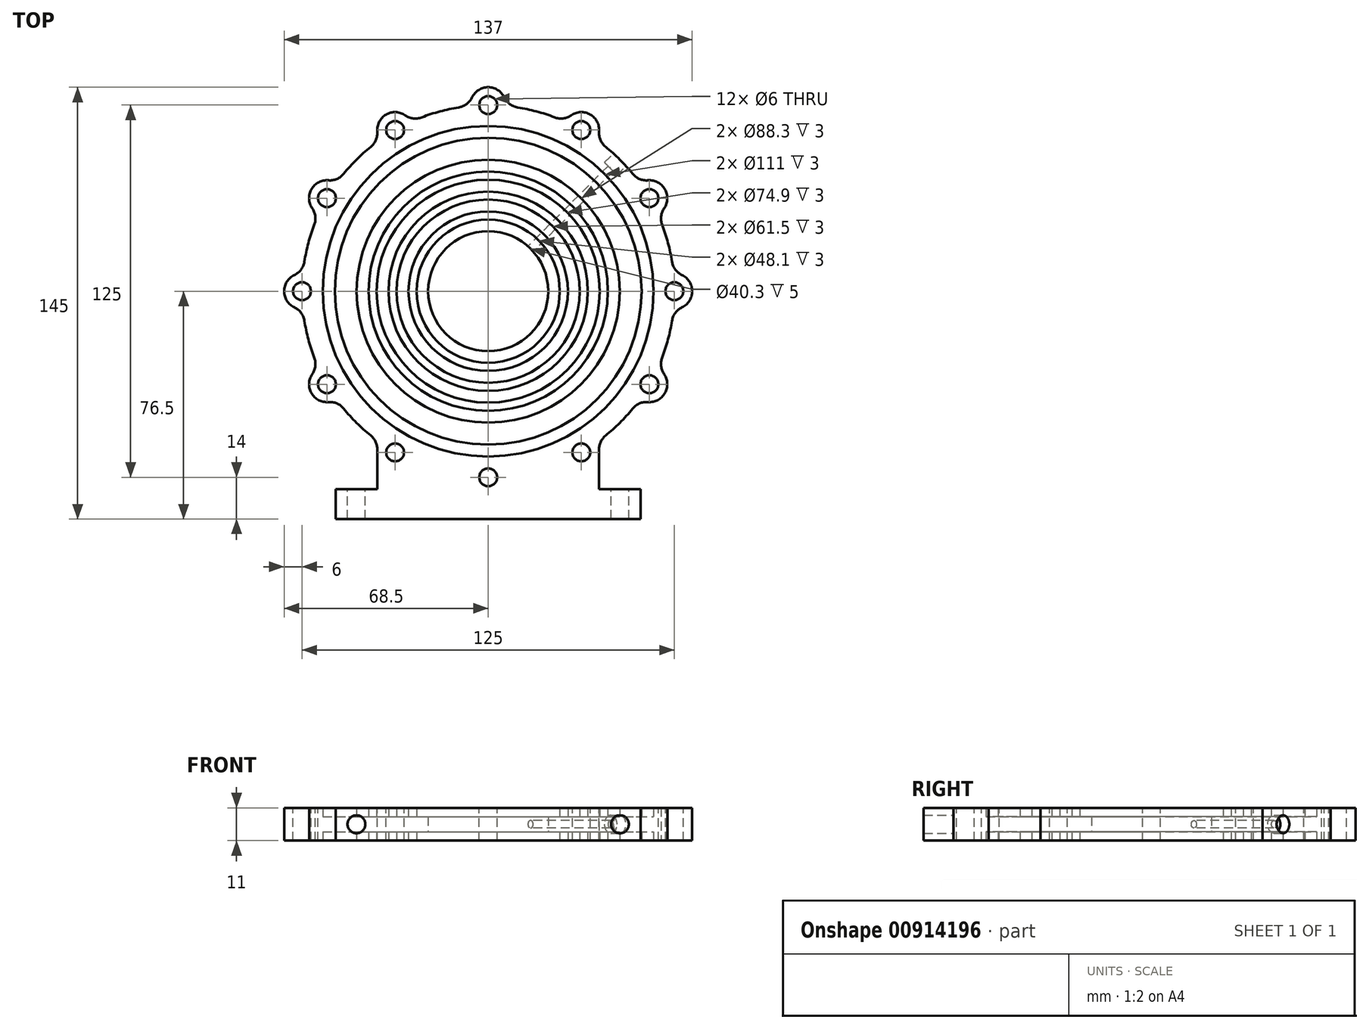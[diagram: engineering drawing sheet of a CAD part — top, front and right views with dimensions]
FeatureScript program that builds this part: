
annotation { "Feature Type Name" : "Feature", "Feature Type Description" : "" }
export const myFeature = defineFeature(function(context is Context, id is Id, definition is map)
    precondition{}
    {
        {
            var Q0;
            Q0=qCreatedBy(makeId("Front.planeOp"),FACE);
            var sketch = newSketch(context, id + "F0", { "sketchPlane" : qUnion([Q0])});
            skLineSegment(sketch, "E0", {"start": v(0, 7.63) * mm, "end": v(0, -7.62) * mm, "construction": true});
            skLineSegment(sketch, "E1", {"start": v(12.5, -2.15) * mm, "end": v(47.5, -2.15) * mm, "construction": true});
            skLineSegment(sketch, "E2", {"start": v(47.5, -2.15) * mm, "end": v(47.5, -0.65) * mm, "construction": true});
            skLineSegment(sketch, "E3", {"start": v(47.5, -0.65) * mm, "end": v(43.5, -0.65) * mm, "construction": true});
            skLineSegment(sketch, "E4", {"start": v(43.5, -0.65) * mm, "end": v(43.5, 2.35) * mm, "construction": true});
            skLineSegment(sketch, "E5", {"start": v(43.5, 2.35) * mm, "end": v(40.8, 2.35) * mm, "construction": true});
            skLineSegment(sketch, "E6", {"start": v(40.8, 2.35) * mm, "end": v(40.8, -0.65) * mm, "construction": true});
            skLineSegment(sketch, "E7", {"start": v(40.8, -0.65) * mm, "end": v(36.8, -0.65) * mm, "construction": true});
            skLineSegment(sketch, "E8", {"start": v(36.8, -0.65) * mm, "end": v(36.8, 2.35) * mm, "construction": true});
            skLineSegment(sketch, "E9", {"start": v(36.8, 2.35) * mm, "end": v(34.1, 2.35) * mm, "construction": true});
            skLineSegment(sketch, "E10", {"start": v(34.1, 2.35) * mm, "end": v(34.1, -0.65) * mm, "construction": true});
            skLineSegment(sketch, "E11", {"start": v(34.1, -0.65) * mm, "end": v(30.1, -0.65) * mm, "construction": true});
            skLineSegment(sketch, "E12", {"start": v(30.1, -0.65) * mm, "end": v(30.1, 2.35) * mm, "construction": true});
            skLineSegment(sketch, "E13", {"start": v(30.1, 2.35) * mm, "end": v(27.4, 2.35) * mm, "construction": true});
            skLineSegment(sketch, "E14", {"start": v(27.4, 2.35) * mm, "end": v(27.4, -0.65) * mm, "construction": true});
            skLineSegment(sketch, "E15", {"start": v(27.4, -0.65) * mm, "end": v(23.4, -0.65) * mm, "construction": true});
            skLineSegment(sketch, "E16", {"start": v(23.4, -0.65) * mm, "end": v(23.4, 2.35) * mm, "construction": true});
            skLineSegment(sketch, "E17", {"start": v(23.4, 2.35) * mm, "end": v(19.5, 2.35) * mm, "construction": true});
            skLineSegment(sketch, "E18", {"start": v(19.5, 2.35) * mm, "end": v(19.5, -0.65) * mm, "construction": true});
            skLineSegment(sketch, "E19", {"start": v(19.5, -0.65) * mm, "end": v(12.5, -0.65) * mm, "construction": true});
            skLineSegment(sketch, "E20", {"start": v(12.5, -0.65) * mm, "end": v(12.5, -2.15) * mm, "construction": true});
            skLineSegment(sketch, "E21.0", {"start": v(24.05, 3) * mm, "end": v(20.15, 3) * mm});
            skLineSegment(sketch, "E21.1", {"start": v(24.05, 0) * mm, "end": v(24.05, 3) * mm});
            skLineSegment(sketch, "E21.2", {"start": v(26.75, 0) * mm, "end": v(24.05, 0) * mm});
            skLineSegment(sketch, "E21.3", {"start": v(26.75, 3) * mm, "end": v(26.75, 0) * mm});
            skLineSegment(sketch, "E21.4", {"start": v(30.75, 3) * mm, "end": v(26.75, 3) * mm});
            skLineSegment(sketch, "E21.5", {"start": v(40.15, 3) * mm, "end": v(40.15, 0) * mm});
            skLineSegment(sketch, "E21.6", {"start": v(44.15, 3) * mm, "end": v(40.15, 3) * mm});
            skLineSegment(sketch, "E21.7", {"start": v(44.15, 0) * mm, "end": v(44.15, 3) * mm});
            skLineSegment(sketch, "E21.8", {"start": v(62.5, 0) * mm, "end": v(55.5, 0) * mm});
            skLineSegment(sketch, "E21.9", {"start": v(40.15, 0) * mm, "end": v(37.45, 0) * mm});
            skLineSegment(sketch, "E21.10", {"start": v(37.45, 0) * mm, "end": v(37.45, 3) * mm});
            skLineSegment(sketch, "E21.11", {"start": v(37.45, 3) * mm, "end": v(33.45, 3) * mm});
            skLineSegment(sketch, "E21.12", {"start": v(33.45, 3) * mm, "end": v(33.45, 0) * mm});
            skLineSegment(sketch, "E21.13", {"start": v(33.45, 0) * mm, "end": v(30.75, 0) * mm});
            skLineSegment(sketch, "E21.14", {"start": v(30.75, 0) * mm, "end": v(30.75, 3) * mm});
            skLineSegment(sketch, "E22", {"start": v(51.5, 0) * mm, "end": v(51.5, 3) * mm});
            skLineSegment(sketch, "E23", {"start": v(51.5, 3) * mm, "end": v(55.5, 3) * mm});
            skLineSegment(sketch, "E24", {"start": v(55.5, 3) * mm, "end": v(55.5, 0) * mm});
            skLineSegment(sketch, "E25.trimOffspring", {"start": v(51.5, 0) * mm, "end": v(44.15, 0) * mm});
            skLineSegment(sketch, "E26", {"start": v(20.15, 5.5) * mm, "end": v(20.15, 3) * mm});
            skLineSegment(sketch, "E27", {"start": v(62.5, 5.5) * mm, "end": v(62.5, 0) * mm});
            skLineSegment(sketch, "E28", {"start": v(20.15, 5.5) * mm, "end": v(62.5, 5.5) * mm, "construction": true});
            skLineSegment(sketch, "E29.MirrorCS", {"start": v(0, 3.37) * mm, "end": v(0, 18.62) * mm, "construction": true});
            skLineSegment(sketch, "E30.MirrorCS", {"start": v(47.5, 13.15) * mm, "end": v(47.5, 11.65) * mm, "construction": true});
            skLineSegment(sketch, "E31.MirrorCS", {"start": v(12.5, 13.15) * mm, "end": v(47.5, 13.15) * mm, "construction": true});
            skLineSegment(sketch, "E32.MirrorCS", {"start": v(26.75, 8) * mm, "end": v(26.75, 11) * mm});
            skLineSegment(sketch, "E33.MirrorCS", {"start": v(23.4, 8.65) * mm, "end": v(19.5, 8.65) * mm, "construction": true});
            skLineSegment(sketch, "E34.MirrorCS", {"start": v(36.8, 8.65) * mm, "end": v(34.1, 8.65) * mm, "construction": true});
            skLineSegment(sketch, "E35.MirrorCS", {"start": v(27.4, 8.65) * mm, "end": v(27.4, 11.65) * mm, "construction": true});
            skLineSegment(sketch, "E36.MirrorCS", {"start": v(37.45, 8) * mm, "end": v(33.45, 8) * mm});
            skLineSegment(sketch, "E37.MirrorCS", {"start": v(20.15, 5.5) * mm, "end": v(20.15, 8) * mm});
            skLineSegment(sketch, "E38.MirrorCS", {"start": v(40.15, 8) * mm, "end": v(40.15, 11) * mm});
            skLineSegment(sketch, "E39.MirrorCS", {"start": v(44.15, 8) * mm, "end": v(40.15, 8) * mm});
            skLineSegment(sketch, "E40.MirrorCS", {"start": v(33.45, 8) * mm, "end": v(33.45, 11) * mm});
            skLineSegment(sketch, "E41.MirrorCS", {"start": v(24.05, 8) * mm, "end": v(20.15, 8) * mm});
            skLineSegment(sketch, "E42.MirrorCS", {"start": v(36.8, 11.65) * mm, "end": v(36.8, 8.65) * mm, "construction": true});
            skLineSegment(sketch, "E43.MirrorCS", {"start": v(40.15, 11) * mm, "end": v(37.45, 11) * mm});
            skLineSegment(sketch, "E44.MirrorCS", {"start": v(24.05, 11) * mm, "end": v(24.05, 8) * mm});
            skLineSegment(sketch, "E45.MirrorCS", {"start": v(12.5, 11.65) * mm, "end": v(12.5, 13.15) * mm, "construction": true});
            skLineSegment(sketch, "E46.MirrorCS", {"start": v(30.1, 8.65) * mm, "end": v(27.4, 8.65) * mm, "construction": true});
            skLineSegment(sketch, "E47.MirrorCS", {"start": v(30.75, 11) * mm, "end": v(30.75, 8) * mm});
            skLineSegment(sketch, "E48.MirrorCS", {"start": v(43.5, 11.65) * mm, "end": v(43.5, 8.65) * mm, "construction": true});
            skLineSegment(sketch, "E49.MirrorCS", {"start": v(55.5, 8) * mm, "end": v(55.5, 11) * mm});
            skLineSegment(sketch, "E50.MirrorCS", {"start": v(34.1, 11.65) * mm, "end": v(30.1, 11.65) * mm, "construction": true});
            skLineSegment(sketch, "E51.MirrorCS", {"start": v(40.8, 8.65) * mm, "end": v(40.8, 11.65) * mm, "construction": true});
            skLineSegment(sketch, "E52.MirrorCS", {"start": v(62.5, 5.5) * mm, "end": v(62.5, 11) * mm});
            skLineSegment(sketch, "E53.MirrorCS", {"start": v(37.45, 11) * mm, "end": v(37.45, 8) * mm});
            skLineSegment(sketch, "E54.MirrorCS", {"start": v(30.75, 8) * mm, "end": v(26.75, 8) * mm});
            skLineSegment(sketch, "E55.MirrorCS", {"start": v(23.4, 11.65) * mm, "end": v(23.4, 8.65) * mm, "construction": true});
            skLineSegment(sketch, "E56.MirrorCS", {"start": v(40.8, 11.65) * mm, "end": v(36.8, 11.65) * mm, "construction": true});
            skLineSegment(sketch, "E57.MirrorCS", {"start": v(47.5, 11.65) * mm, "end": v(43.5, 11.65) * mm, "construction": true});
            skLineSegment(sketch, "E58.MirrorCS", {"start": v(19.5, 8.65) * mm, "end": v(19.5, 11.65) * mm, "construction": true});
            skLineSegment(sketch, "E59.MirrorCS", {"start": v(30.1, 11.65) * mm, "end": v(30.1, 8.65) * mm, "construction": true});
            skLineSegment(sketch, "E60.MirrorCS", {"start": v(27.4, 11.65) * mm, "end": v(23.4, 11.65) * mm, "construction": true});
            skLineSegment(sketch, "E61.MirrorCS", {"start": v(26.75, 11) * mm, "end": v(24.05, 11) * mm});
            skLineSegment(sketch, "E62.MirrorCS", {"start": v(51.5, 11) * mm, "end": v(51.5, 8) * mm});
            skLineSegment(sketch, "E63.MirrorCS", {"start": v(51.5, 11) * mm, "end": v(44.15, 11) * mm});
            skLineSegment(sketch, "E64.MirrorCS", {"start": v(51.5, 8) * mm, "end": v(55.5, 8) * mm});
            skLineSegment(sketch, "E65.MirrorCS", {"start": v(44.15, 11) * mm, "end": v(44.15, 8) * mm});
            skLineSegment(sketch, "E66.MirrorCS", {"start": v(62.5, 11) * mm, "end": v(55.5, 11) * mm});
            skLineSegment(sketch, "E67.MirrorCS", {"start": v(34.1, 8.65) * mm, "end": v(34.1, 11.65) * mm, "construction": true});
            skLineSegment(sketch, "E68.MirrorCS", {"start": v(19.5, 11.65) * mm, "end": v(12.5, 11.65) * mm, "construction": true});
            skLineSegment(sketch, "E69.MirrorCS", {"start": v(33.45, 11) * mm, "end": v(30.75, 11) * mm});
            skLineSegment(sketch, "E70.MirrorCS", {"start": v(43.5, 8.65) * mm, "end": v(40.8, 8.65) * mm, "construction": true});
            skLineSegment(sketch, "E71", {"start": v(59.5, 11) * mm, "end": v(59.5, 0) * mm, "construction": true});
            skSolve(sketch);
        }
        {
            var Q0;
            Q0 = qSketchRegion(id + "F0", true);
            var Q1;
            Q1=sQuery(id+"F0.wireOp",EDGE,"E29.MirrorCS");
            revolve(context, id + "F1", {"surfaceOperationType" : NewSurfaceOperationType.NEW, "entities" : qUnion([Q0]), "axis" : qUnion([Q1]), "revolveType" : RevolveType.FULL});
        }
        {
            var Q0;
            Q0=makeQuery(id+"F1.opRevolve","SWEPT_FACE",FACE,{"disambiguationData":[OSD([sQuery(id+"F0.wireOp",EDGE,"E66.MirrorCS")])]});
            var sketch = newSketch(context, id + "F2", { "sketchPlane" : qUnion([Q0])});
            skCircle(sketch, "E72", {"center": v(0, 62.5) * mm, "radius": 6 * mm});
            skCircle(sketch, "E73.1.0", {"center": v(-31.25, 54.13) * mm, "radius": 6 * mm});
            skCircle(sketch, "E73.2.0", {"center": v(-54.13, 31.25) * mm, "radius": 6 * mm});
            skCircle(sketch, "E73.3.0", {"center": v(-62.5, 0) * mm, "radius": 6 * mm});
            skCircle(sketch, "E73.4.0", {"center": v(-54.13, -31.25) * mm, "radius": 6 * mm});
            skCircle(sketch, "E73.5.0", {"center": v(-31.25, -54.13) * mm, "radius": 6 * mm});
            skCircle(sketch, "E73.6.0", {"center": v(0, -62.5) * mm, "radius": 6 * mm});
            skCircle(sketch, "E73.7.0", {"center": v(31.25, -54.13) * mm, "radius": 6 * mm});
            skCircle(sketch, "E73.8.0", {"center": v(54.13, -31.25) * mm, "radius": 6 * mm});
            skCircle(sketch, "E73.9.0", {"center": v(62.5, 0) * mm, "radius": 6 * mm});
            skCircle(sketch, "E73.10.0", {"center": v(54.13, 31.25) * mm, "radius": 6 * mm});
            skCircle(sketch, "E73.11.0", {"center": v(31.25, 54.13) * mm, "radius": 6 * mm});
            skPoint(sketch, "E73.center", {"position": v(0, 0) * mm});
            skSolve(sketch);
        }
        {
            var Q0;
            Q0 = qSketchRegion(id + "F2", true);
            var Q1;
            Q1=makeQuery(id+"F1.opRevolve","SWEPT_FACE",FACE,{"disambiguationData":[OSD([sQuery(id+"F0.wireOp",EDGE,"E21.8")])]});
            extrude(context, id + "F3", {"entities" : qUnion([Q0]), "operationType" : NewBodyOperationType.ADD, "endBound" : BoundingType.UP_TO_SURFACE, "oppositeDirection" : true, "depth" : 10 * mm, "endBoundEntityFace" : qUnion([Q1]), "offsetDistance" : 25 * mm});
        }
        {
            var Q0;
            Q0=makeQuery(id+"F3.boolean.opBoolean","MERGE",FACE,{"derivedFrom":[makeQuery(id+"F1.opRevolve","SWEPT_FACE",FACE,{"disambiguationData":[OSD([sQuery(id+"F0.wireOp",EDGE,"E66.MirrorCS")])]}),makeQuery(id+"F3.opExtrude","CAP_FACE",FACE,{"disambiguationData":[OSD([sQuery(id+"F2.wireOp",EDGE,"E72")])],"isStart":true}),makeQuery(id+"F3.opExtrude","CAP_FACE",FACE,{"disambiguationData":[OSD([sQuery(id+"F2.wireOp",EDGE,"E73.1.0")])],"isStart":true}),makeQuery(id+"F3.opExtrude","CAP_FACE",FACE,{"disambiguationData":[OSD([sQuery(id+"F2.wireOp",EDGE,"E73.2.0")])],"isStart":true}),makeQuery(id+"F3.opExtrude","CAP_FACE",FACE,{"disambiguationData":[OSD([sQuery(id+"F2.wireOp",EDGE,"E73.3.0")])],"isStart":true}),makeQuery(id+"F3.opExtrude","CAP_FACE",FACE,{"disambiguationData":[OSD([sQuery(id+"F2.wireOp",EDGE,"E73.4.0")])],"isStart":true}),makeQuery(id+"F3.opExtrude","CAP_FACE",FACE,{"disambiguationData":[OSD([sQuery(id+"F2.wireOp",EDGE,"E73.5.0")])],"isStart":true}),makeQuery(id+"F3.opExtrude","CAP_FACE",FACE,{"disambiguationData":[OSD([sQuery(id+"F2.wireOp",EDGE,"E73.6.0")])],"isStart":true}),makeQuery(id+"F3.opExtrude","CAP_FACE",FACE,{"disambiguationData":[OSD([sQuery(id+"F2.wireOp",EDGE,"E73.7.0")])],"isStart":true}),makeQuery(id+"F3.opExtrude","CAP_FACE",FACE,{"disambiguationData":[OSD([sQuery(id+"F2.wireOp",EDGE,"E73.8.0")])],"isStart":true}),makeQuery(id+"F3.opExtrude","CAP_FACE",FACE,{"disambiguationData":[OSD([sQuery(id+"F2.wireOp",EDGE,"E73.9.0")])],"isStart":true}),makeQuery(id+"F3.opExtrude","CAP_FACE",FACE,{"disambiguationData":[OSD([sQuery(id+"F2.wireOp",EDGE,"E73.10.0")])],"isStart":true}),makeQuery(id+"F3.opExtrude","CAP_FACE",FACE,{"disambiguationData":[OSD([sQuery(id+"F2.wireOp",EDGE,"E73.11.0")])],"isStart":true})]});
            var sketch = newSketch(context, id + "F4", { "sketchPlane" : qUnion([Q0])});
            skCircle(sketch, "E74", {"center": v(0, 62.5) * mm, "radius": 3 * mm});
            skCircle(sketch, "E75.1.0", {"center": v(-31.25, 54.13) * mm, "radius": 3 * mm});
            skCircle(sketch, "E75.2.0", {"center": v(-54.13, 31.25) * mm, "radius": 3 * mm});
            skCircle(sketch, "E75.3.0", {"center": v(-62.5, 0) * mm, "radius": 3 * mm});
            skCircle(sketch, "E75.4.0", {"center": v(-54.13, -31.25) * mm, "radius": 3 * mm});
            skCircle(sketch, "E75.5.0", {"center": v(-31.25, -54.13) * mm, "radius": 3 * mm});
            skCircle(sketch, "E75.6.0", {"center": v(0, -62.5) * mm, "radius": 3 * mm});
            skCircle(sketch, "E75.7.0", {"center": v(31.25, -54.13) * mm, "radius": 3 * mm});
            skCircle(sketch, "E75.8.0", {"center": v(54.13, -31.25) * mm, "radius": 3 * mm});
            skCircle(sketch, "E75.9.0", {"center": v(62.5, 0) * mm, "radius": 3 * mm});
            skCircle(sketch, "E75.10.0", {"center": v(54.13, 31.25) * mm, "radius": 3 * mm});
            skCircle(sketch, "E75.11.0", {"center": v(31.25, 54.13) * mm, "radius": 3 * mm});
            skPoint(sketch, "E75.center", {"position": v(0, 0) * mm});
            skSolve(sketch);
        }
        {
            var Q0;
            Q0 = qSketchRegion(id + "F4", true);
            extrude(context, id + "F5", {"entities" : qUnion([Q0]), "operationType" : NewBodyOperationType.REMOVE, "endBound" : BoundingType.THROUGH_ALL, "oppositeDirection" : true, "depth" : 25 * mm, "offsetDistance" : 25 * mm});
        }
        {
            var Q0;
            Q0=makeQuery(id+"F3.boolean.opBoolean","INTERSECT",EDGE,{"disambiguationData":[OD(1.0)],"derivedFrom":[makeQuery(id+"F1.opRevolve","SWEPT_FACE",FACE,{"disambiguationData":[OSD([sQuery(id+"F0.wireOp",EDGE,"E27"),sQuery(id+"F0.wireOp",EDGE,"E52.MirrorCS")])]}),makeQuery(id+"F3.opExtrude","SWEPT_FACE",FACE,{"disambiguationData":[OSD([sQuery(id+"F2.wireOp",EDGE,"E73.8.0")])]})]});
            var Q1;
            Q1=makeQuery(id+"F3.boolean.opBoolean","INTERSECT",EDGE,{"disambiguationData":[OD(1.0)],"derivedFrom":[makeQuery(id+"F1.opRevolve","SWEPT_FACE",FACE,{"disambiguationData":[OSD([sQuery(id+"F0.wireOp",EDGE,"E27"),sQuery(id+"F0.wireOp",EDGE,"E52.MirrorCS")])]}),makeQuery(id+"F3.opExtrude","SWEPT_FACE",FACE,{"disambiguationData":[OSD([sQuery(id+"F2.wireOp",EDGE,"E73.7.0")])]})]});
            var Q2;
            Q2=makeQuery(id+"F3.boolean.opBoolean","INTERSECT",EDGE,{"disambiguationData":[OD(0.0)],"derivedFrom":[makeQuery(id+"F1.opRevolve","SWEPT_FACE",FACE,{"disambiguationData":[OSD([sQuery(id+"F0.wireOp",EDGE,"E27"),sQuery(id+"F0.wireOp",EDGE,"E52.MirrorCS")])]}),makeQuery(id+"F3.opExtrude","SWEPT_FACE",FACE,{"disambiguationData":[OSD([sQuery(id+"F2.wireOp",EDGE,"E73.9.0")])]})]});
            var Q3;
            Q3=makeQuery(id+"F3.boolean.opBoolean","INTERSECT",EDGE,{"disambiguationData":[OD(1.0)],"derivedFrom":[makeQuery(id+"F1.opRevolve","SWEPT_FACE",FACE,{"disambiguationData":[OSD([sQuery(id+"F0.wireOp",EDGE,"E27"),sQuery(id+"F0.wireOp",EDGE,"E52.MirrorCS")])]}),makeQuery(id+"F3.opExtrude","SWEPT_FACE",FACE,{"disambiguationData":[OSD([sQuery(id+"F2.wireOp",EDGE,"E73.9.0")])]})]});
            var Q4;
            Q4=makeQuery(id+"F3.boolean.opBoolean","INTERSECT",EDGE,{"disambiguationData":[OD(0.0)],"derivedFrom":[makeQuery(id+"F1.opRevolve","SWEPT_FACE",FACE,{"disambiguationData":[OSD([sQuery(id+"F0.wireOp",EDGE,"E27"),sQuery(id+"F0.wireOp",EDGE,"E52.MirrorCS")])]}),makeQuery(id+"F3.opExtrude","SWEPT_FACE",FACE,{"disambiguationData":[OSD([sQuery(id+"F2.wireOp",EDGE,"E73.8.0")])]})]});
            var Q5;
            Q5=makeQuery(id+"F3.boolean.opBoolean","INTERSECT",EDGE,{"disambiguationData":[OD(0.0)],"derivedFrom":[makeQuery(id+"F1.opRevolve","SWEPT_FACE",FACE,{"disambiguationData":[OSD([sQuery(id+"F0.wireOp",EDGE,"E27"),sQuery(id+"F0.wireOp",EDGE,"E52.MirrorCS")])]}),makeQuery(id+"F3.opExtrude","SWEPT_FACE",FACE,{"disambiguationData":[OSD([sQuery(id+"F2.wireOp",EDGE,"E73.7.0")])]})]});
            var Q6;
            Q6=makeQuery(id+"F3.boolean.opBoolean","INTERSECT",EDGE,{"disambiguationData":[OD(1.0)],"derivedFrom":[makeQuery(id+"F1.opRevolve","SWEPT_FACE",FACE,{"disambiguationData":[OSD([sQuery(id+"F0.wireOp",EDGE,"E27"),sQuery(id+"F0.wireOp",EDGE,"E52.MirrorCS")])]}),makeQuery(id+"F3.opExtrude","SWEPT_FACE",FACE,{"disambiguationData":[OSD([sQuery(id+"F2.wireOp",EDGE,"E73.6.0")])]})]});
            var Q7;
            Q7=makeQuery(id+"F3.boolean.opBoolean","INTERSECT",EDGE,{"disambiguationData":[OD(1.0)],"derivedFrom":[makeQuery(id+"F1.opRevolve","SWEPT_FACE",FACE,{"disambiguationData":[OSD([sQuery(id+"F0.wireOp",EDGE,"E27"),sQuery(id+"F0.wireOp",EDGE,"E52.MirrorCS")])]}),makeQuery(id+"F3.opExtrude","SWEPT_FACE",FACE,{"disambiguationData":[OSD([sQuery(id+"F2.wireOp",EDGE,"E73.5.0")])]})]});
            var Q8;
            Q8=makeQuery(id+"F3.boolean.opBoolean","INTERSECT",EDGE,{"disambiguationData":[OD(0.0)],"derivedFrom":[makeQuery(id+"F1.opRevolve","SWEPT_FACE",FACE,{"disambiguationData":[OSD([sQuery(id+"F0.wireOp",EDGE,"E27"),sQuery(id+"F0.wireOp",EDGE,"E52.MirrorCS")])]}),makeQuery(id+"F3.opExtrude","SWEPT_FACE",FACE,{"disambiguationData":[OSD([sQuery(id+"F2.wireOp",EDGE,"E73.6.0")])]})]});
            var Q9;
            Q9=makeQuery(id+"F3.boolean.opBoolean","INTERSECT",EDGE,{"disambiguationData":[OD(0.0)],"derivedFrom":[makeQuery(id+"F1.opRevolve","SWEPT_FACE",FACE,{"disambiguationData":[OSD([sQuery(id+"F0.wireOp",EDGE,"E27"),sQuery(id+"F0.wireOp",EDGE,"E52.MirrorCS")])]}),makeQuery(id+"F3.opExtrude","SWEPT_FACE",FACE,{"disambiguationData":[OSD([sQuery(id+"F2.wireOp",EDGE,"E73.5.0")])]})]});
            var Q10;
            Q10=makeQuery(id+"F3.boolean.opBoolean","INTERSECT",EDGE,{"disambiguationData":[OD(0.0)],"derivedFrom":[makeQuery(id+"F1.opRevolve","SWEPT_FACE",FACE,{"disambiguationData":[OSD([sQuery(id+"F0.wireOp",EDGE,"E27"),sQuery(id+"F0.wireOp",EDGE,"E52.MirrorCS")])]}),makeQuery(id+"F3.opExtrude","SWEPT_FACE",FACE,{"disambiguationData":[OSD([sQuery(id+"F2.wireOp",EDGE,"E73.4.0")])]})]});
            var Q11;
            Q11=makeQuery(id+"F3.boolean.opBoolean","INTERSECT",EDGE,{"disambiguationData":[OD(1.0)],"derivedFrom":[makeQuery(id+"F1.opRevolve","SWEPT_FACE",FACE,{"disambiguationData":[OSD([sQuery(id+"F0.wireOp",EDGE,"E27"),sQuery(id+"F0.wireOp",EDGE,"E52.MirrorCS")])]}),makeQuery(id+"F3.opExtrude","SWEPT_FACE",FACE,{"disambiguationData":[OSD([sQuery(id+"F2.wireOp",EDGE,"E73.4.0")])]})]});
            var Q12;
            Q12=makeQuery(id+"F3.boolean.opBoolean","INTERSECT",EDGE,{"disambiguationData":[OD(0.0)],"derivedFrom":[makeQuery(id+"F1.opRevolve","SWEPT_FACE",FACE,{"disambiguationData":[OSD([sQuery(id+"F0.wireOp",EDGE,"E27"),sQuery(id+"F0.wireOp",EDGE,"E52.MirrorCS")])]}),makeQuery(id+"F3.opExtrude","SWEPT_FACE",FACE,{"disambiguationData":[OSD([sQuery(id+"F2.wireOp",EDGE,"E73.2.0")])]})]});
            var Q13;
            Q13=makeQuery(id+"F3.boolean.opBoolean","INTERSECT",EDGE,{"disambiguationData":[OD(0.0)],"derivedFrom":[makeQuery(id+"F1.opRevolve","SWEPT_FACE",FACE,{"disambiguationData":[OSD([sQuery(id+"F0.wireOp",EDGE,"E27"),sQuery(id+"F0.wireOp",EDGE,"E52.MirrorCS")])]}),makeQuery(id+"F3.opExtrude","SWEPT_FACE",FACE,{"disambiguationData":[OSD([sQuery(id+"F2.wireOp",EDGE,"E73.3.0")])]})]});
            var Q14;
            Q14=makeQuery(id+"F3.boolean.opBoolean","INTERSECT",EDGE,{"disambiguationData":[OD(1.0)],"derivedFrom":[makeQuery(id+"F1.opRevolve","SWEPT_FACE",FACE,{"disambiguationData":[OSD([sQuery(id+"F0.wireOp",EDGE,"E27"),sQuery(id+"F0.wireOp",EDGE,"E52.MirrorCS")])]}),makeQuery(id+"F3.opExtrude","SWEPT_FACE",FACE,{"disambiguationData":[OSD([sQuery(id+"F2.wireOp",EDGE,"E73.2.0")])]})]});
            var Q15;
            Q15=makeQuery(id+"F3.boolean.opBoolean","INTERSECT",EDGE,{"disambiguationData":[OD(1.0)],"derivedFrom":[makeQuery(id+"F1.opRevolve","SWEPT_FACE",FACE,{"disambiguationData":[OSD([sQuery(id+"F0.wireOp",EDGE,"E27"),sQuery(id+"F0.wireOp",EDGE,"E52.MirrorCS")])]}),makeQuery(id+"F3.opExtrude","SWEPT_FACE",FACE,{"disambiguationData":[OSD([sQuery(id+"F2.wireOp",EDGE,"E73.3.0")])]})]});
            var Q16;
            Q16=makeQuery(id+"F3.boolean.opBoolean","INTERSECT",EDGE,{"disambiguationData":[OD(0.0)],"derivedFrom":[makeQuery(id+"F1.opRevolve","SWEPT_FACE",FACE,{"disambiguationData":[OSD([sQuery(id+"F0.wireOp",EDGE,"E27"),sQuery(id+"F0.wireOp",EDGE,"E52.MirrorCS")])]}),makeQuery(id+"F3.opExtrude","SWEPT_FACE",FACE,{"disambiguationData":[OSD([sQuery(id+"F2.wireOp",EDGE,"E73.1.0")])]})]});
            var Q17;
            Q17=makeQuery(id+"F3.boolean.opBoolean","INTERSECT",EDGE,{"disambiguationData":[OD(1.0)],"derivedFrom":[makeQuery(id+"F1.opRevolve","SWEPT_FACE",FACE,{"disambiguationData":[OSD([sQuery(id+"F0.wireOp",EDGE,"E27"),sQuery(id+"F0.wireOp",EDGE,"E52.MirrorCS")])]}),makeQuery(id+"F3.opExtrude","SWEPT_FACE",FACE,{"disambiguationData":[OSD([sQuery(id+"F2.wireOp",EDGE,"E72")])]})]});
            var Q18;
            Q18=makeQuery(id+"F3.boolean.opBoolean","INTERSECT",EDGE,{"disambiguationData":[OD(1.0)],"derivedFrom":[makeQuery(id+"F1.opRevolve","SWEPT_FACE",FACE,{"disambiguationData":[OSD([sQuery(id+"F0.wireOp",EDGE,"E27"),sQuery(id+"F0.wireOp",EDGE,"E52.MirrorCS")])]}),makeQuery(id+"F3.opExtrude","SWEPT_FACE",FACE,{"disambiguationData":[OSD([sQuery(id+"F2.wireOp",EDGE,"E73.11.0")])]})]});
            var Q19;
            Q19=makeQuery(id+"F3.boolean.opBoolean","INTERSECT",EDGE,{"disambiguationData":[OD(1.0)],"derivedFrom":[makeQuery(id+"F1.opRevolve","SWEPT_FACE",FACE,{"disambiguationData":[OSD([sQuery(id+"F0.wireOp",EDGE,"E27"),sQuery(id+"F0.wireOp",EDGE,"E52.MirrorCS")])]}),makeQuery(id+"F3.opExtrude","SWEPT_FACE",FACE,{"disambiguationData":[OSD([sQuery(id+"F2.wireOp",EDGE,"E73.10.0")])]})]});
            var Q20;
            Q20=makeQuery(id+"F3.boolean.opBoolean","INTERSECT",EDGE,{"disambiguationData":[OD(0.0)],"derivedFrom":[makeQuery(id+"F1.opRevolve","SWEPT_FACE",FACE,{"disambiguationData":[OSD([sQuery(id+"F0.wireOp",EDGE,"E27"),sQuery(id+"F0.wireOp",EDGE,"E52.MirrorCS")])]}),makeQuery(id+"F3.opExtrude","SWEPT_FACE",FACE,{"disambiguationData":[OSD([sQuery(id+"F2.wireOp",EDGE,"E73.10.0")])]})]});
            var Q21;
            Q21=makeQuery(id+"F3.boolean.opBoolean","INTERSECT",EDGE,{"disambiguationData":[OD(0.0)],"derivedFrom":[makeQuery(id+"F1.opRevolve","SWEPT_FACE",FACE,{"disambiguationData":[OSD([sQuery(id+"F0.wireOp",EDGE,"E27"),sQuery(id+"F0.wireOp",EDGE,"E52.MirrorCS")])]}),makeQuery(id+"F3.opExtrude","SWEPT_FACE",FACE,{"disambiguationData":[OSD([sQuery(id+"F2.wireOp",EDGE,"E73.11.0")])]})]});
            var Q22;
            Q22=makeQuery(id+"F3.boolean.opBoolean","INTERSECT",EDGE,{"disambiguationData":[OD(0.0)],"derivedFrom":[makeQuery(id+"F1.opRevolve","SWEPT_FACE",FACE,{"disambiguationData":[OSD([sQuery(id+"F0.wireOp",EDGE,"E27"),sQuery(id+"F0.wireOp",EDGE,"E52.MirrorCS")])]}),makeQuery(id+"F3.opExtrude","SWEPT_FACE",FACE,{"disambiguationData":[OSD([sQuery(id+"F2.wireOp",EDGE,"E72")])]})]});
            var Q23;
            Q23=makeQuery(id+"F3.boolean.opBoolean","INTERSECT",EDGE,{"disambiguationData":[OD(1.0)],"derivedFrom":[makeQuery(id+"F1.opRevolve","SWEPT_FACE",FACE,{"disambiguationData":[OSD([sQuery(id+"F0.wireOp",EDGE,"E27"),sQuery(id+"F0.wireOp",EDGE,"E52.MirrorCS")])]}),makeQuery(id+"F3.opExtrude","SWEPT_FACE",FACE,{"disambiguationData":[OSD([sQuery(id+"F2.wireOp",EDGE,"E73.1.0")])]})]});
            fillet(context, id + "F6", {"entities" : qUnion([Q0, Q1, Q2, Q3, Q4, Q5, Q6, Q7, Q8, Q9, Q10, Q11, Q12, Q13, Q14, Q15, Q16, Q17, Q18, Q19, Q20, Q21, Q22, Q23]), "radius" : 6 * mm, "tangentPropagation" : true, "allowEdgeOverflow" : false});
        }
        {
            var Q0;
            Q0=makeQuery(id+"F3.boolean.opBoolean","MERGE",FACE,{"derivedFrom":[makeQuery(id+"F1.opRevolve","SWEPT_FACE",FACE,{"disambiguationData":[OSD([sQuery(id+"F0.wireOp",EDGE,"E66.MirrorCS")])]}),makeQuery(id+"F3.opExtrude","CAP_FACE",FACE,{"disambiguationData":[OSD([sQuery(id+"F2.wireOp",EDGE,"E72")])],"isStart":true}),makeQuery(id+"F3.opExtrude","CAP_FACE",FACE,{"disambiguationData":[OSD([sQuery(id+"F2.wireOp",EDGE,"E73.1.0")])],"isStart":true}),makeQuery(id+"F3.opExtrude","CAP_FACE",FACE,{"disambiguationData":[OSD([sQuery(id+"F2.wireOp",EDGE,"E73.2.0")])],"isStart":true}),makeQuery(id+"F3.opExtrude","CAP_FACE",FACE,{"disambiguationData":[OSD([sQuery(id+"F2.wireOp",EDGE,"E73.3.0")])],"isStart":true}),makeQuery(id+"F3.opExtrude","CAP_FACE",FACE,{"disambiguationData":[OSD([sQuery(id+"F2.wireOp",EDGE,"E73.4.0")])],"isStart":true}),makeQuery(id+"F3.opExtrude","CAP_FACE",FACE,{"disambiguationData":[OSD([sQuery(id+"F2.wireOp",EDGE,"E73.5.0")])],"isStart":true}),makeQuery(id+"F3.opExtrude","CAP_FACE",FACE,{"disambiguationData":[OSD([sQuery(id+"F2.wireOp",EDGE,"E73.6.0")])],"isStart":true}),makeQuery(id+"F3.opExtrude","CAP_FACE",FACE,{"disambiguationData":[OSD([sQuery(id+"F2.wireOp",EDGE,"E73.7.0")])],"isStart":true}),makeQuery(id+"F3.opExtrude","CAP_FACE",FACE,{"disambiguationData":[OSD([sQuery(id+"F2.wireOp",EDGE,"E73.8.0")])],"isStart":true}),makeQuery(id+"F3.opExtrude","CAP_FACE",FACE,{"disambiguationData":[OSD([sQuery(id+"F2.wireOp",EDGE,"E73.9.0")])],"isStart":true}),makeQuery(id+"F3.opExtrude","CAP_FACE",FACE,{"disambiguationData":[OSD([sQuery(id+"F2.wireOp",EDGE,"E73.10.0")])],"isStart":true}),makeQuery(id+"F3.opExtrude","CAP_FACE",FACE,{"disambiguationData":[OSD([sQuery(id+"F2.wireOp",EDGE,"E73.11.0")])],"isStart":true})]});
            var sketch = newSketch(context, id + "F7", { "sketchPlane" : qUnion([Q0])});
            skLineSegment(sketch, "E76", {"start": v(-37.23, -53.64) * mm, "end": v(-37.23, -66.5) * mm});
            skLineSegment(sketch, "E77", {"start": v(-37.23, -66.5) * mm, "end": v(-51.23, -66.5) * mm});
            skLineSegment(sketch, "E78", {"start": v(-51.23, -66.5) * mm, "end": v(-51.23, -76.5) * mm});
            skLineSegment(sketch, "E79", {"start": v(-51.23, -76.5) * mm, "end": v(0, -76.5) * mm});
            skLineSegment(sketch, "E80", {"start": v(0, -76.5) * mm, "end": v(0, -68.5) * mm});
            skLineSegment(sketch, "E81.MirrorCS", {"start": v(37.23, -53.64) * mm, "end": v(37.23, -66.5) * mm});
            skLineSegment(sketch, "E82.MirrorCS", {"start": v(37.23, -66.5) * mm, "end": v(51.23, -66.5) * mm});
            skLineSegment(sketch, "E83.MirrorCS", {"start": v(51.23, -66.5) * mm, "end": v(51.23, -76.5) * mm});
            skLineSegment(sketch, "E84.MirrorCS", {"start": v(51.23, -76.5) * mm, "end": v(0, -76.5) * mm});
            skSolve(sketch);
        }
        {
            var Q0;
            {var subQ24=sQuery(id+"F7.wireOp",EDGE,"E77");Q0=makeQuery(id+"F7.imprint","IMPRINT",FACE,{"disambiguationData":[TD([[makeQuery(id+"F7.imprint","IMPRINT",EDGE,{"derivedFrom":subQ24}),1.0]])]});}
            var Q1;
            {var subQ26=sQuery(id+"F7.wireOp",EDGE,"E80");Q1=makeQuery(id+"F7.imprint","IMPRINT",FACE,{"disambiguationData":[TD([[makeQuery(id+"F7.imprint","IMPRINT",EDGE,{"derivedFrom":subQ26}),-1.0]])]});}
            var Q2;
            Q2=qCreatedBy(makeId("Top.planeOp"),FACE);
            extrude(context, id + "F8", {"entities" : qUnion([Q0, Q1]), "operationType" : NewBodyOperationType.ADD, "endBound" : BoundingType.UP_TO_SURFACE, "oppositeDirection" : true, "depth" : 25 * mm, "endBoundEntityFace" : qUnion([Q2]), "offsetDistance" : 25 * mm});
        }
        {
            var Q0;
            Q0=makeQuery(id+"F8.opExtrude","SWEPT_FACE",FACE,{"disambiguationData":[OSD([sQuery(id+"F7.wireOp",EDGE,"E82.MirrorCS")])]});
            var sketch = newSketch(context, id + "F9", { "sketchPlane" : qUnion([Q0])});
            skPoint(sketch, "E85", {"position": v(-44.23, 5.5) * mm});
            skPoint(sketch, "E85.positionSnap0", {"position": v(-51.23, 5.5) * mm});
            skPoint(sketch, "E85.positionSnap1", {"position": v(-44.23, 11) * mm});
            skCircle(sketch, "E86", {"center": v(-44.23, 5.5) * mm, "radius": 3 * mm});
            skCircle(sketch, "E87.MirrorC", {"center": v(44.23, 5.5) * mm, "radius": 3 * mm});
            skSolve(sketch);
        }
        {
            var Q0;
            Q0 = qSketchRegion(id + "F9", true);
            extrude(context, id + "F10", {"entities" : qUnion([Q0]), "operationType" : NewBodyOperationType.REMOVE, "endBound" : BoundingType.THROUGH_ALL, "oppositeDirection" : true, "depth" : 25 * mm, "offsetDistance" : 25 * mm});
        }
        {
            var Q0;
            {var subQ0=sQuery(id+"F2.wireOp",EDGE,"E73.9.0");var subQ1=sQuery(id+"F2.wireOp",EDGE,"E73.8.0");var subQ2=sQuery(id+"F2.wireOp",EDGE,"E73.7.0");var subQ3=sQuery(id+"F2.wireOp",EDGE,"E73.6.0");var subQ4=sQuery(id+"F2.wireOp",EDGE,"E73.5.0");var subQ5=sQuery(id+"F2.wireOp",EDGE,"E73.4.0");var subQ6=sQuery(id+"F2.wireOp",EDGE,"E72");var subQ7=sQuery(id+"F2.wireOp",EDGE,"E73.1.0");var subQ8=sQuery(id+"F2.wireOp",EDGE,"E73.2.0");var subQ9=sQuery(id+"F2.wireOp",EDGE,"E73.3.0");var subQ10=sQuery(id+"F2.wireOp",EDGE,"E73.10.0");var subQ11=sQuery(id+"F2.wireOp",EDGE,"E73.11.0");var subQ12=makeQuery(id+"F3.opExtrude","SWEPT_FACE",FACE,{"disambiguationData":[OSD([subQ11])]});var subQ13=makeQuery(id+"F1.opRevolve","SWEPT_FACE",FACE,{"disambiguationData":[OSD([sQuery(id+"F0.wireOp",EDGE,"E27"),sQuery(id+"F0.wireOp",EDGE,"E52.MirrorCS")])]});Q0=makeQuery(id+"F6.opFillet","BLEND_EDGE",EDGE,{"blendedFrom":[makeQuery(id+"F3.boolean.opBoolean","INTERSECT",EDGE,{"disambiguationData":[OD(1.0)],"derivedFrom":[subQ13,subQ12]}),makeQuery(id+"F3.boolean.opBoolean","SPLIT",FACE,{"disambiguationData":[TD([makeQuery(id+"F1.opRevolve","SWEPT_FACE",FACE,{"disambiguationData":[OSD([sQuery(id+"F0.wireOp",EDGE,"E21.8")])]}),makeQuery(id+"F1.opRevolve","SWEPT_FACE",FACE,{"disambiguationData":[OSD([sQuery(id+"F0.wireOp",EDGE,"E66.MirrorCS")])]}),makeQuery(id+"F3.opExtrude","CAP_FACE",FACE,{"disambiguationData":[OSD([subQ6])],"isStart":true}),makeQuery(id+"F3.opExtrude","CAP_FACE",FACE,{"disambiguationData":[OSD([subQ6])],"isStart":false}),makeQuery(id+"F3.opExtrude","CAP_FACE",FACE,{"disambiguationData":[OSD([subQ7])],"isStart":true}),makeQuery(id+"F3.opExtrude","CAP_FACE",FACE,{"disambiguationData":[OSD([subQ7])],"isStart":false}),makeQuery(id+"F3.opExtrude","CAP_FACE",FACE,{"disambiguationData":[OSD([subQ8])],"isStart":true}),makeQuery(id+"F3.opExtrude","CAP_FACE",FACE,{"disambiguationData":[OSD([subQ8])],"isStart":false}),makeQuery(id+"F3.opExtrude","CAP_FACE",FACE,{"disambiguationData":[OSD([subQ9])],"isStart":true}),makeQuery(id+"F3.opExtrude","CAP_FACE",FACE,{"disambiguationData":[OSD([subQ9])],"isStart":false}),makeQuery(id+"F3.opExtrude","CAP_FACE",FACE,{"disambiguationData":[OSD([subQ5])],"isStart":true}),makeQuery(id+"F3.opExtrude","CAP_FACE",FACE,{"disambiguationData":[OSD([subQ5])],"isStart":false}),makeQuery(id+"F3.opExtrude","CAP_FACE",FACE,{"disambiguationData":[OSD([subQ4])],"isStart":true}),makeQuery(id+"F3.opExtrude","CAP_FACE",FACE,{"disambiguationData":[OSD([subQ4])],"isStart":false}),makeQuery(id+"F3.opExtrude","CAP_FACE",FACE,{"disambiguationData":[OSD([subQ3])],"isStart":true}),makeQuery(id+"F3.opExtrude","CAP_FACE",FACE,{"disambiguationData":[OSD([subQ3])],"isStart":false}),makeQuery(id+"F3.opExtrude","CAP_FACE",FACE,{"disambiguationData":[OSD([subQ2])],"isStart":true}),makeQuery(id+"F3.opExtrude","CAP_FACE",FACE,{"disambiguationData":[OSD([subQ2])],"isStart":false}),makeQuery(id+"F3.opExtrude","CAP_FACE",FACE,{"disambiguationData":[OSD([subQ1])],"isStart":true}),makeQuery(id+"F3.opExtrude","CAP_FACE",FACE,{"disambiguationData":[OSD([subQ1])],"isStart":false}),makeQuery(id+"F3.opExtrude","CAP_FACE",FACE,{"disambiguationData":[OSD([subQ0])],"isStart":true}),makeQuery(id+"F3.opExtrude","CAP_FACE",FACE,{"disambiguationData":[OSD([subQ0])],"isStart":false}),makeQuery(id+"F3.opExtrude","SWEPT_FACE",FACE,{"disambiguationData":[OSD([subQ10])]}),makeQuery(id+"F3.opExtrude","CAP_FACE",FACE,{"disambiguationData":[OSD([subQ10])],"isStart":true}),makeQuery(id+"F3.opExtrude","CAP_FACE",FACE,{"disambiguationData":[OSD([subQ10])],"isStart":false}),subQ12,makeQuery(id+"F3.opExtrude","CAP_FACE",FACE,{"disambiguationData":[OSD([subQ11])],"isStart":true}),makeQuery(id+"F3.opExtrude","CAP_FACE",FACE,{"disambiguationData":[OSD([subQ11])],"isStart":false})])],"derivedFrom":subQ13})],"blendedInto":[makeQuery(id+"F3.boolean.opBoolean","SPLIT",FACE,{"disambiguationData":[TD([makeQuery(id+"F1.opRevolve","SWEPT_FACE",FACE,{"disambiguationData":[OSD([sQuery(id+"F0.wireOp",EDGE,"E21.8")])]}),makeQuery(id+"F1.opRevolve","SWEPT_FACE",FACE,{"disambiguationData":[OSD([sQuery(id+"F0.wireOp",EDGE,"E66.MirrorCS")])]}),makeQuery(id+"F3.opExtrude","CAP_FACE",FACE,{"disambiguationData":[OSD([subQ6])],"isStart":true}),makeQuery(id+"F3.opExtrude","CAP_FACE",FACE,{"disambiguationData":[OSD([subQ6])],"isStart":false}),makeQuery(id+"F3.opExtrude","CAP_FACE",FACE,{"disambiguationData":[OSD([subQ7])],"isStart":true}),makeQuery(id+"F3.opExtrude","CAP_FACE",FACE,{"disambiguationData":[OSD([subQ7])],"isStart":false}),makeQuery(id+"F3.opExtrude","CAP_FACE",FACE,{"disambiguationData":[OSD([subQ8])],"isStart":true}),makeQuery(id+"F3.opExtrude","CAP_FACE",FACE,{"disambiguationData":[OSD([subQ8])],"isStart":false}),makeQuery(id+"F3.opExtrude","CAP_FACE",FACE,{"disambiguationData":[OSD([subQ9])],"isStart":true}),makeQuery(id+"F3.opExtrude","CAP_FACE",FACE,{"disambiguationData":[OSD([subQ9])],"isStart":false}),makeQuery(id+"F3.opExtrude","CAP_FACE",FACE,{"disambiguationData":[OSD([subQ5])],"isStart":true}),makeQuery(id+"F3.opExtrude","CAP_FACE",FACE,{"disambiguationData":[OSD([subQ5])],"isStart":false}),makeQuery(id+"F3.opExtrude","CAP_FACE",FACE,{"disambiguationData":[OSD([subQ4])],"isStart":true}),makeQuery(id+"F3.opExtrude","CAP_FACE",FACE,{"disambiguationData":[OSD([subQ4])],"isStart":false}),makeQuery(id+"F3.opExtrude","CAP_FACE",FACE,{"disambiguationData":[OSD([subQ3])],"isStart":true}),makeQuery(id+"F3.opExtrude","CAP_FACE",FACE,{"disambiguationData":[OSD([subQ3])],"isStart":false}),makeQuery(id+"F3.opExtrude","CAP_FACE",FACE,{"disambiguationData":[OSD([subQ2])],"isStart":true}),makeQuery(id+"F3.opExtrude","CAP_FACE",FACE,{"disambiguationData":[OSD([subQ2])],"isStart":false}),makeQuery(id+"F3.opExtrude","CAP_FACE",FACE,{"disambiguationData":[OSD([subQ1])],"isStart":true}),makeQuery(id+"F3.opExtrude","CAP_FACE",FACE,{"disambiguationData":[OSD([subQ1])],"isStart":false}),makeQuery(id+"F3.opExtrude","CAP_FACE",FACE,{"disambiguationData":[OSD([subQ0])],"isStart":true}),makeQuery(id+"F3.opExtrude","CAP_FACE",FACE,{"disambiguationData":[OSD([subQ0])],"isStart":false}),makeQuery(id+"F3.opExtrude","SWEPT_FACE",FACE,{"disambiguationData":[OSD([subQ10])]}),makeQuery(id+"F3.opExtrude","CAP_FACE",FACE,{"disambiguationData":[OSD([subQ10])],"isStart":true}),makeQuery(id+"F3.opExtrude","CAP_FACE",FACE,{"disambiguationData":[OSD([subQ10])],"isStart":false}),subQ12,makeQuery(id+"F3.opExtrude","CAP_FACE",FACE,{"disambiguationData":[OSD([subQ11])],"isStart":true}),makeQuery(id+"F3.opExtrude","CAP_FACE",FACE,{"disambiguationData":[OSD([subQ11])],"isStart":false})])],"derivedFrom":subQ13})]});}
            cPoint(context, id + "F11", {"entities" : qUnion([Q0]), "parameter" : 0.5});
        }
        {
            var Q0;
            {var subQ0=sQuery(id+"F2.wireOp",EDGE,"E73.9.0");var subQ1=sQuery(id+"F2.wireOp",EDGE,"E73.8.0");var subQ2=sQuery(id+"F2.wireOp",EDGE,"E73.7.0");var subQ3=sQuery(id+"F2.wireOp",EDGE,"E73.6.0");var subQ4=sQuery(id+"F2.wireOp",EDGE,"E73.5.0");var subQ5=sQuery(id+"F2.wireOp",EDGE,"E73.4.0");var subQ6=sQuery(id+"F2.wireOp",EDGE,"E72");var subQ7=sQuery(id+"F2.wireOp",EDGE,"E73.1.0");var subQ8=sQuery(id+"F2.wireOp",EDGE,"E73.2.0");var subQ9=sQuery(id+"F2.wireOp",EDGE,"E73.3.0");var subQ10=sQuery(id+"F2.wireOp",EDGE,"E73.10.0");var subQ11=makeQuery(id+"F3.opExtrude","SWEPT_FACE",FACE,{"disambiguationData":[OSD([subQ10])]});var subQ12=sQuery(id+"F2.wireOp",EDGE,"E73.11.0");var subQ13=makeQuery(id+"F1.opRevolve","SWEPT_FACE",FACE,{"disambiguationData":[OSD([sQuery(id+"F0.wireOp",EDGE,"E27"),sQuery(id+"F0.wireOp",EDGE,"E52.MirrorCS")])]});Q0=makeQuery(id+"F6.opFillet","BLEND_EDGE",EDGE,{"blendedFrom":[makeQuery(id+"F3.boolean.opBoolean","INTERSECT",EDGE,{"disambiguationData":[OD(1.0)],"derivedFrom":[subQ13,subQ11]}),makeQuery(id+"F3.boolean.opBoolean","SPLIT",FACE,{"disambiguationData":[TD([makeQuery(id+"F1.opRevolve","SWEPT_FACE",FACE,{"disambiguationData":[OSD([sQuery(id+"F0.wireOp",EDGE,"E21.8")])]}),makeQuery(id+"F1.opRevolve","SWEPT_FACE",FACE,{"disambiguationData":[OSD([sQuery(id+"F0.wireOp",EDGE,"E66.MirrorCS")])]}),makeQuery(id+"F3.opExtrude","CAP_FACE",FACE,{"disambiguationData":[OSD([subQ6])],"isStart":true}),makeQuery(id+"F3.opExtrude","CAP_FACE",FACE,{"disambiguationData":[OSD([subQ6])],"isStart":false}),makeQuery(id+"F3.opExtrude","CAP_FACE",FACE,{"disambiguationData":[OSD([subQ7])],"isStart":true}),makeQuery(id+"F3.opExtrude","CAP_FACE",FACE,{"disambiguationData":[OSD([subQ7])],"isStart":false}),makeQuery(id+"F3.opExtrude","CAP_FACE",FACE,{"disambiguationData":[OSD([subQ8])],"isStart":true}),makeQuery(id+"F3.opExtrude","CAP_FACE",FACE,{"disambiguationData":[OSD([subQ8])],"isStart":false}),makeQuery(id+"F3.opExtrude","CAP_FACE",FACE,{"disambiguationData":[OSD([subQ9])],"isStart":true}),makeQuery(id+"F3.opExtrude","CAP_FACE",FACE,{"disambiguationData":[OSD([subQ9])],"isStart":false}),makeQuery(id+"F3.opExtrude","CAP_FACE",FACE,{"disambiguationData":[OSD([subQ5])],"isStart":true}),makeQuery(id+"F3.opExtrude","CAP_FACE",FACE,{"disambiguationData":[OSD([subQ5])],"isStart":false}),makeQuery(id+"F3.opExtrude","CAP_FACE",FACE,{"disambiguationData":[OSD([subQ4])],"isStart":true}),makeQuery(id+"F3.opExtrude","CAP_FACE",FACE,{"disambiguationData":[OSD([subQ4])],"isStart":false}),makeQuery(id+"F3.opExtrude","CAP_FACE",FACE,{"disambiguationData":[OSD([subQ3])],"isStart":true}),makeQuery(id+"F3.opExtrude","CAP_FACE",FACE,{"disambiguationData":[OSD([subQ3])],"isStart":false}),makeQuery(id+"F3.opExtrude","CAP_FACE",FACE,{"disambiguationData":[OSD([subQ2])],"isStart":true}),makeQuery(id+"F3.opExtrude","CAP_FACE",FACE,{"disambiguationData":[OSD([subQ2])],"isStart":false}),makeQuery(id+"F3.opExtrude","CAP_FACE",FACE,{"disambiguationData":[OSD([subQ1])],"isStart":true}),makeQuery(id+"F3.opExtrude","CAP_FACE",FACE,{"disambiguationData":[OSD([subQ1])],"isStart":false}),makeQuery(id+"F3.opExtrude","CAP_FACE",FACE,{"disambiguationData":[OSD([subQ0])],"isStart":true}),makeQuery(id+"F3.opExtrude","CAP_FACE",FACE,{"disambiguationData":[OSD([subQ0])],"isStart":false}),subQ11,makeQuery(id+"F3.opExtrude","CAP_FACE",FACE,{"disambiguationData":[OSD([subQ10])],"isStart":true}),makeQuery(id+"F3.opExtrude","CAP_FACE",FACE,{"disambiguationData":[OSD([subQ10])],"isStart":false}),makeQuery(id+"F3.opExtrude","SWEPT_FACE",FACE,{"disambiguationData":[OSD([subQ12])]}),makeQuery(id+"F3.opExtrude","CAP_FACE",FACE,{"disambiguationData":[OSD([subQ12])],"isStart":true}),makeQuery(id+"F3.opExtrude","CAP_FACE",FACE,{"disambiguationData":[OSD([subQ12])],"isStart":false})])],"derivedFrom":subQ13})],"blendedInto":[makeQuery(id+"F3.boolean.opBoolean","SPLIT",FACE,{"disambiguationData":[TD([makeQuery(id+"F1.opRevolve","SWEPT_FACE",FACE,{"disambiguationData":[OSD([sQuery(id+"F0.wireOp",EDGE,"E21.8")])]}),makeQuery(id+"F1.opRevolve","SWEPT_FACE",FACE,{"disambiguationData":[OSD([sQuery(id+"F0.wireOp",EDGE,"E66.MirrorCS")])]}),makeQuery(id+"F3.opExtrude","CAP_FACE",FACE,{"disambiguationData":[OSD([subQ6])],"isStart":true}),makeQuery(id+"F3.opExtrude","CAP_FACE",FACE,{"disambiguationData":[OSD([subQ6])],"isStart":false}),makeQuery(id+"F3.opExtrude","CAP_FACE",FACE,{"disambiguationData":[OSD([subQ7])],"isStart":true}),makeQuery(id+"F3.opExtrude","CAP_FACE",FACE,{"disambiguationData":[OSD([subQ7])],"isStart":false}),makeQuery(id+"F3.opExtrude","CAP_FACE",FACE,{"disambiguationData":[OSD([subQ8])],"isStart":true}),makeQuery(id+"F3.opExtrude","CAP_FACE",FACE,{"disambiguationData":[OSD([subQ8])],"isStart":false}),makeQuery(id+"F3.opExtrude","CAP_FACE",FACE,{"disambiguationData":[OSD([subQ9])],"isStart":true}),makeQuery(id+"F3.opExtrude","CAP_FACE",FACE,{"disambiguationData":[OSD([subQ9])],"isStart":false}),makeQuery(id+"F3.opExtrude","CAP_FACE",FACE,{"disambiguationData":[OSD([subQ5])],"isStart":true}),makeQuery(id+"F3.opExtrude","CAP_FACE",FACE,{"disambiguationData":[OSD([subQ5])],"isStart":false}),makeQuery(id+"F3.opExtrude","CAP_FACE",FACE,{"disambiguationData":[OSD([subQ4])],"isStart":true}),makeQuery(id+"F3.opExtrude","CAP_FACE",FACE,{"disambiguationData":[OSD([subQ4])],"isStart":false}),makeQuery(id+"F3.opExtrude","CAP_FACE",FACE,{"disambiguationData":[OSD([subQ3])],"isStart":true}),makeQuery(id+"F3.opExtrude","CAP_FACE",FACE,{"disambiguationData":[OSD([subQ3])],"isStart":false}),makeQuery(id+"F3.opExtrude","CAP_FACE",FACE,{"disambiguationData":[OSD([subQ2])],"isStart":true}),makeQuery(id+"F3.opExtrude","CAP_FACE",FACE,{"disambiguationData":[OSD([subQ2])],"isStart":false}),makeQuery(id+"F3.opExtrude","CAP_FACE",FACE,{"disambiguationData":[OSD([subQ1])],"isStart":true}),makeQuery(id+"F3.opExtrude","CAP_FACE",FACE,{"disambiguationData":[OSD([subQ1])],"isStart":false}),makeQuery(id+"F3.opExtrude","CAP_FACE",FACE,{"disambiguationData":[OSD([subQ0])],"isStart":true}),makeQuery(id+"F3.opExtrude","CAP_FACE",FACE,{"disambiguationData":[OSD([subQ0])],"isStart":false}),subQ11,makeQuery(id+"F3.opExtrude","CAP_FACE",FACE,{"disambiguationData":[OSD([subQ10])],"isStart":true}),makeQuery(id+"F3.opExtrude","CAP_FACE",FACE,{"disambiguationData":[OSD([subQ10])],"isStart":false}),makeQuery(id+"F3.opExtrude","SWEPT_FACE",FACE,{"disambiguationData":[OSD([subQ12])]}),makeQuery(id+"F3.opExtrude","CAP_FACE",FACE,{"disambiguationData":[OSD([subQ12])],"isStart":true}),makeQuery(id+"F3.opExtrude","CAP_FACE",FACE,{"disambiguationData":[OSD([subQ12])],"isStart":false})])],"derivedFrom":subQ13})]});}
            cPoint(context, id + "F12", {"entities" : qUnion([Q0]), "parameter" : 0.5});
        }
        {
            var Q0;
            {var subQ0=sQuery(id+"F2.wireOp",EDGE,"E73.11.0");var subQ1=makeQuery(id+"F3.opExtrude","CAP_FACE",FACE,{"disambiguationData":[OSD([subQ0])],"isStart":false});var subQ2=sQuery(id+"F2.wireOp",EDGE,"E73.10.0");var subQ3=makeQuery(id+"F3.opExtrude","CAP_FACE",FACE,{"disambiguationData":[OSD([subQ2])],"isStart":false});var subQ4=sQuery(id+"F2.wireOp",EDGE,"E73.9.0");var subQ5=makeQuery(id+"F3.opExtrude","CAP_FACE",FACE,{"disambiguationData":[OSD([subQ4])],"isStart":false});var subQ6=sQuery(id+"F2.wireOp",EDGE,"E73.8.0");var subQ7=makeQuery(id+"F3.opExtrude","CAP_FACE",FACE,{"disambiguationData":[OSD([subQ6])],"isStart":false});var subQ8=sQuery(id+"F2.wireOp",EDGE,"E73.7.0");var subQ9=makeQuery(id+"F3.opExtrude","CAP_FACE",FACE,{"disambiguationData":[OSD([subQ8])],"isStart":false});var subQ10=sQuery(id+"F2.wireOp",EDGE,"E73.6.0");var subQ11=makeQuery(id+"F3.opExtrude","CAP_FACE",FACE,{"disambiguationData":[OSD([subQ10])],"isStart":false});var subQ12=sQuery(id+"F2.wireOp",EDGE,"E73.5.0");var subQ13=makeQuery(id+"F3.opExtrude","CAP_FACE",FACE,{"disambiguationData":[OSD([subQ12])],"isStart":false});var subQ14=sQuery(id+"F2.wireOp",EDGE,"E73.4.0");var subQ15=makeQuery(id+"F3.opExtrude","CAP_FACE",FACE,{"disambiguationData":[OSD([subQ14])],"isStart":false});var subQ16=sQuery(id+"F2.wireOp",EDGE,"E73.3.0");var subQ17=makeQuery(id+"F3.opExtrude","CAP_FACE",FACE,{"disambiguationData":[OSD([subQ16])],"isStart":false});var subQ18=sQuery(id+"F2.wireOp",EDGE,"E73.2.0");var subQ19=makeQuery(id+"F3.opExtrude","CAP_FACE",FACE,{"disambiguationData":[OSD([subQ18])],"isStart":false});var subQ20=sQuery(id+"F2.wireOp",EDGE,"E73.1.0");var subQ21=makeQuery(id+"F3.opExtrude","CAP_FACE",FACE,{"disambiguationData":[OSD([subQ20])],"isStart":false});var subQ22=sQuery(id+"F2.wireOp",EDGE,"E72");var subQ23=makeQuery(id+"F3.opExtrude","CAP_FACE",FACE,{"disambiguationData":[OSD([subQ22])],"isStart":false});var subQ24=makeQuery(id+"F1.opRevolve","SWEPT_FACE",FACE,{"disambiguationData":[OSD([sQuery(id+"F0.wireOp",EDGE,"E21.8")])]});var subQ25=makeQuery(id+"F3.opExtrude","SWEPT_FACE",FACE,{"disambiguationData":[OSD([subQ0])]});var subQ26=makeQuery(id+"F1.opRevolve","SWEPT_FACE",FACE,{"disambiguationData":[OSD([sQuery(id+"F0.wireOp",EDGE,"E27"),sQuery(id+"F0.wireOp",EDGE,"E52.MirrorCS")])]});Q0=makeQuery(id+"F6.opFillet","BLEND_VERTEX",VERTEX,{"blendedFrom":[makeQuery(id+"F3.boolean.opBoolean","INTERSECT",EDGE,{"disambiguationData":[OD(1.0)],"derivedFrom":[subQ26,subQ25]}),makeQuery(id+"F3.boolean.opBoolean","SPLIT",FACE,{"disambiguationData":[TD([subQ24,makeQuery(id+"F1.opRevolve","SWEPT_FACE",FACE,{"disambiguationData":[OSD([sQuery(id+"F0.wireOp",EDGE,"E66.MirrorCS")])]}),makeQuery(id+"F3.opExtrude","CAP_FACE",FACE,{"disambiguationData":[OSD([subQ22])],"isStart":true}),subQ23,makeQuery(id+"F3.opExtrude","CAP_FACE",FACE,{"disambiguationData":[OSD([subQ20])],"isStart":true}),subQ21,makeQuery(id+"F3.opExtrude","CAP_FACE",FACE,{"disambiguationData":[OSD([subQ18])],"isStart":true}),subQ19,makeQuery(id+"F3.opExtrude","CAP_FACE",FACE,{"disambiguationData":[OSD([subQ16])],"isStart":true}),subQ17,makeQuery(id+"F3.opExtrude","CAP_FACE",FACE,{"disambiguationData":[OSD([subQ14])],"isStart":true}),subQ15,makeQuery(id+"F3.opExtrude","CAP_FACE",FACE,{"disambiguationData":[OSD([subQ12])],"isStart":true}),subQ13,makeQuery(id+"F3.opExtrude","CAP_FACE",FACE,{"disambiguationData":[OSD([subQ10])],"isStart":true}),subQ11,makeQuery(id+"F3.opExtrude","CAP_FACE",FACE,{"disambiguationData":[OSD([subQ8])],"isStart":true}),subQ9,makeQuery(id+"F3.opExtrude","CAP_FACE",FACE,{"disambiguationData":[OSD([subQ6])],"isStart":true}),subQ7,makeQuery(id+"F3.opExtrude","CAP_FACE",FACE,{"disambiguationData":[OSD([subQ4])],"isStart":true}),subQ5,makeQuery(id+"F3.opExtrude","SWEPT_FACE",FACE,{"disambiguationData":[OSD([subQ2])]}),makeQuery(id+"F3.opExtrude","CAP_FACE",FACE,{"disambiguationData":[OSD([subQ2])],"isStart":true}),subQ3,subQ25,makeQuery(id+"F3.opExtrude","CAP_FACE",FACE,{"disambiguationData":[OSD([subQ0])],"isStart":true}),subQ1])],"derivedFrom":subQ26}),makeQuery(id+"F3.boolean.opBoolean","MERGE",FACE,{"derivedFrom":[subQ24,subQ23,subQ21,subQ19,subQ17,subQ15,subQ13,subQ11,subQ9,subQ7,subQ5,subQ3,subQ1]})],"blendedInto":[makeQuery(id+"F3.boolean.opBoolean","SPLIT",FACE,{"disambiguationData":[TD([subQ24,makeQuery(id+"F1.opRevolve","SWEPT_FACE",FACE,{"disambiguationData":[OSD([sQuery(id+"F0.wireOp",EDGE,"E66.MirrorCS")])]}),makeQuery(id+"F3.opExtrude","CAP_FACE",FACE,{"disambiguationData":[OSD([subQ22])],"isStart":true}),subQ23,makeQuery(id+"F3.opExtrude","CAP_FACE",FACE,{"disambiguationData":[OSD([subQ20])],"isStart":true}),subQ21,makeQuery(id+"F3.opExtrude","CAP_FACE",FACE,{"disambiguationData":[OSD([subQ18])],"isStart":true}),subQ19,makeQuery(id+"F3.opExtrude","CAP_FACE",FACE,{"disambiguationData":[OSD([subQ16])],"isStart":true}),subQ17,makeQuery(id+"F3.opExtrude","CAP_FACE",FACE,{"disambiguationData":[OSD([subQ14])],"isStart":true}),subQ15,makeQuery(id+"F3.opExtrude","CAP_FACE",FACE,{"disambiguationData":[OSD([subQ12])],"isStart":true}),subQ13,makeQuery(id+"F3.opExtrude","CAP_FACE",FACE,{"disambiguationData":[OSD([subQ10])],"isStart":true}),subQ11,makeQuery(id+"F3.opExtrude","CAP_FACE",FACE,{"disambiguationData":[OSD([subQ8])],"isStart":true}),subQ9,makeQuery(id+"F3.opExtrude","CAP_FACE",FACE,{"disambiguationData":[OSD([subQ6])],"isStart":true}),subQ7,makeQuery(id+"F3.opExtrude","CAP_FACE",FACE,{"disambiguationData":[OSD([subQ4])],"isStart":true}),subQ5,makeQuery(id+"F3.opExtrude","SWEPT_FACE",FACE,{"disambiguationData":[OSD([subQ2])]}),makeQuery(id+"F3.opExtrude","CAP_FACE",FACE,{"disambiguationData":[OSD([subQ2])],"isStart":true}),subQ3,subQ25,makeQuery(id+"F3.opExtrude","CAP_FACE",FACE,{"disambiguationData":[OSD([subQ0])],"isStart":true}),subQ1])],"derivedFrom":subQ26}),makeQuery(id+"F3.boolean.opBoolean","MERGE",FACE,{"derivedFrom":[subQ24,subQ23,subQ21,subQ19,subQ17,subQ15,subQ13,subQ11,subQ9,subQ7,subQ5,subQ3,subQ1]})]});}
            var Q1;
            Q1 = qCreatedBy(id + "F11" ,VERTEX);
            var Q2;
            Q2 = qCreatedBy(id + "F12" ,VERTEX);
            cPlane(context, id + "F13", {"entities" : qUnion([Q0, Q1, Q2]), "cplaneType" : CPlaneType.THREE_POINT, "offset" : 25 * mm, "width" : 150 * mm, "height" : 150 * mm});
        }
        {
            var Q0;
            Q0=qCreatedBy(id+"F13.planeOp",FACE);
            var sketch = newSketch(context, id + "F14", { "sketchPlane" : qUnion([Q0])});
            skPoint(sketch, "E88.0", {"position": v(-6.41, 5.5) * mm});
            skCircle(sketch, "E89", {"center": v(0, 5.5) * mm, "radius": 1.25 * mm});
            skSolve(sketch);
        }
        {
            var Q0;
            Q0 = qSketchRegion(id + "F14", true);
            var Q1;
            {var subQ0=sQuery(id+"F2.wireOp",EDGE,"E73.9.0");var subQ1=sQuery(id+"F2.wireOp",EDGE,"E73.8.0");var subQ2=sQuery(id+"F2.wireOp",EDGE,"E73.7.0");var subQ3=sQuery(id+"F2.wireOp",EDGE,"E73.6.0");var subQ4=sQuery(id+"F2.wireOp",EDGE,"E73.5.0");var subQ5=sQuery(id+"F2.wireOp",EDGE,"E73.4.0");var subQ6=sQuery(id+"F2.wireOp",EDGE,"E72");var subQ7=sQuery(id+"F2.wireOp",EDGE,"E73.1.0");var subQ8=sQuery(id+"F2.wireOp",EDGE,"E73.2.0");var subQ9=sQuery(id+"F2.wireOp",EDGE,"E73.3.0");var subQ10=sQuery(id+"F2.wireOp",EDGE,"E73.10.0");var subQ11=sQuery(id+"F2.wireOp",EDGE,"E73.11.0");Q1=makeQuery(id+"F3.boolean.opBoolean","SPLIT",FACE,{"disambiguationData":[TD([makeQuery(id+"F1.opRevolve","SWEPT_FACE",FACE,{"disambiguationData":[OSD([sQuery(id+"F0.wireOp",EDGE,"E21.8")])]}),makeQuery(id+"F1.opRevolve","SWEPT_FACE",FACE,{"disambiguationData":[OSD([sQuery(id+"F0.wireOp",EDGE,"E66.MirrorCS")])]}),makeQuery(id+"F3.opExtrude","CAP_FACE",FACE,{"disambiguationData":[OSD([subQ6])],"isStart":true}),makeQuery(id+"F3.opExtrude","CAP_FACE",FACE,{"disambiguationData":[OSD([subQ6])],"isStart":false}),makeQuery(id+"F3.opExtrude","CAP_FACE",FACE,{"disambiguationData":[OSD([subQ7])],"isStart":true}),makeQuery(id+"F3.opExtrude","CAP_FACE",FACE,{"disambiguationData":[OSD([subQ7])],"isStart":false}),makeQuery(id+"F3.opExtrude","CAP_FACE",FACE,{"disambiguationData":[OSD([subQ8])],"isStart":true}),makeQuery(id+"F3.opExtrude","CAP_FACE",FACE,{"disambiguationData":[OSD([subQ8])],"isStart":false}),makeQuery(id+"F3.opExtrude","CAP_FACE",FACE,{"disambiguationData":[OSD([subQ9])],"isStart":true}),makeQuery(id+"F3.opExtrude","CAP_FACE",FACE,{"disambiguationData":[OSD([subQ9])],"isStart":false}),makeQuery(id+"F3.opExtrude","CAP_FACE",FACE,{"disambiguationData":[OSD([subQ5])],"isStart":true}),makeQuery(id+"F3.opExtrude","CAP_FACE",FACE,{"disambiguationData":[OSD([subQ5])],"isStart":false}),makeQuery(id+"F3.opExtrude","CAP_FACE",FACE,{"disambiguationData":[OSD([subQ4])],"isStart":true}),makeQuery(id+"F3.opExtrude","CAP_FACE",FACE,{"disambiguationData":[OSD([subQ4])],"isStart":false}),makeQuery(id+"F3.opExtrude","CAP_FACE",FACE,{"disambiguationData":[OSD([subQ3])],"isStart":true}),makeQuery(id+"F3.opExtrude","CAP_FACE",FACE,{"disambiguationData":[OSD([subQ3])],"isStart":false}),makeQuery(id+"F3.opExtrude","CAP_FACE",FACE,{"disambiguationData":[OSD([subQ2])],"isStart":true}),makeQuery(id+"F3.opExtrude","CAP_FACE",FACE,{"disambiguationData":[OSD([subQ2])],"isStart":false}),makeQuery(id+"F3.opExtrude","CAP_FACE",FACE,{"disambiguationData":[OSD([subQ1])],"isStart":true}),makeQuery(id+"F3.opExtrude","CAP_FACE",FACE,{"disambiguationData":[OSD([subQ1])],"isStart":false}),makeQuery(id+"F3.opExtrude","CAP_FACE",FACE,{"disambiguationData":[OSD([subQ0])],"isStart":true}),makeQuery(id+"F3.opExtrude","CAP_FACE",FACE,{"disambiguationData":[OSD([subQ0])],"isStart":false}),makeQuery(id+"F3.opExtrude","SWEPT_FACE",FACE,{"disambiguationData":[OSD([subQ10])]}),makeQuery(id+"F3.opExtrude","CAP_FACE",FACE,{"disambiguationData":[OSD([subQ10])],"isStart":true}),makeQuery(id+"F3.opExtrude","CAP_FACE",FACE,{"disambiguationData":[OSD([subQ10])],"isStart":false}),makeQuery(id+"F3.opExtrude","SWEPT_FACE",FACE,{"disambiguationData":[OSD([subQ11])]}),makeQuery(id+"F3.opExtrude","CAP_FACE",FACE,{"disambiguationData":[OSD([subQ11])],"isStart":true}),makeQuery(id+"F3.opExtrude","CAP_FACE",FACE,{"disambiguationData":[OSD([subQ11])],"isStart":false})])],"derivedFrom":makeQuery(id+"F1.opRevolve","SWEPT_FACE",FACE,{"disambiguationData":[OSD([sQuery(id+"F0.wireOp",EDGE,"E27"),sQuery(id+"F0.wireOp",EDGE,"E52.MirrorCS")])]})});}
            var Q2;
            Q2=makeQuery(id+"F1.opRevolve","SWEPT_FACE",FACE,{"disambiguationData":[OSD([sQuery(id+"F0.wireOp",EDGE,"E26"),sQuery(id+"F0.wireOp",EDGE,"E37.MirrorCS")])]});
            extrude(context, id + "F15", {"entities" : qUnion([Q0]), "operationType" : NewBodyOperationType.REMOVE, "endBound" : BoundingType.UP_TO_SURFACE, "oppositeDirection" : true, "depth" : 25 * mm, "endBoundEntityFace" : qUnion([Q1]), "offsetDistance" : 25 * mm, "hasSecondDirection" : true, "secondDirectionBound" : SecondDirectionBoundingType.UP_TO_SURFACE, "secondDirectionOppositeDirection" : false, "secondDirectionDepth" : 25 * mm, "secondDirectionBoundEntityFace" : qUnion([Q2])});
        }
        {
            var Q0;
            Q0=qCreatedBy(id+"F13.planeOp",FACE);
            var sketch = newSketch(context, id + "F16", { "sketchPlane" : qUnion([Q0])});
            skCircle(sketch, "E90", {"center": v(0, 5.5) * mm, "radius": 3 * mm});
            skCircle(sketch, "E91.0", {"center": v(0, 5.5) * mm, "radius": 1.25 * mm});
            skSolve(sketch);
        }
        {
            var Q0;
            Q0 = qSketchRegion(id + "F16", true);
            var Q1;
            {var subQ0=sQuery(id+"F2.wireOp",EDGE,"E73.9.0");var subQ1=sQuery(id+"F2.wireOp",EDGE,"E73.8.0");var subQ2=sQuery(id+"F2.wireOp",EDGE,"E73.7.0");var subQ3=sQuery(id+"F2.wireOp",EDGE,"E73.6.0");var subQ4=sQuery(id+"F2.wireOp",EDGE,"E73.5.0");var subQ5=sQuery(id+"F2.wireOp",EDGE,"E73.4.0");var subQ6=sQuery(id+"F2.wireOp",EDGE,"E72");var subQ7=sQuery(id+"F2.wireOp",EDGE,"E73.1.0");var subQ8=sQuery(id+"F2.wireOp",EDGE,"E73.2.0");var subQ9=sQuery(id+"F2.wireOp",EDGE,"E73.3.0");var subQ10=sQuery(id+"F2.wireOp",EDGE,"E73.10.0");var subQ11=sQuery(id+"F2.wireOp",EDGE,"E73.11.0");Q1=makeQuery(id+"F3.boolean.opBoolean","SPLIT",FACE,{"disambiguationData":[TD([makeQuery(id+"F1.opRevolve","SWEPT_FACE",FACE,{"disambiguationData":[OSD([sQuery(id+"F0.wireOp",EDGE,"E21.8")])]}),makeQuery(id+"F1.opRevolve","SWEPT_FACE",FACE,{"disambiguationData":[OSD([sQuery(id+"F0.wireOp",EDGE,"E66.MirrorCS")])]}),makeQuery(id+"F3.opExtrude","CAP_FACE",FACE,{"disambiguationData":[OSD([subQ6])],"isStart":true}),makeQuery(id+"F3.opExtrude","CAP_FACE",FACE,{"disambiguationData":[OSD([subQ6])],"isStart":false}),makeQuery(id+"F3.opExtrude","CAP_FACE",FACE,{"disambiguationData":[OSD([subQ7])],"isStart":true}),makeQuery(id+"F3.opExtrude","CAP_FACE",FACE,{"disambiguationData":[OSD([subQ7])],"isStart":false}),makeQuery(id+"F3.opExtrude","CAP_FACE",FACE,{"disambiguationData":[OSD([subQ8])],"isStart":true}),makeQuery(id+"F3.opExtrude","CAP_FACE",FACE,{"disambiguationData":[OSD([subQ8])],"isStart":false}),makeQuery(id+"F3.opExtrude","CAP_FACE",FACE,{"disambiguationData":[OSD([subQ9])],"isStart":true}),makeQuery(id+"F3.opExtrude","CAP_FACE",FACE,{"disambiguationData":[OSD([subQ9])],"isStart":false}),makeQuery(id+"F3.opExtrude","CAP_FACE",FACE,{"disambiguationData":[OSD([subQ5])],"isStart":true}),makeQuery(id+"F3.opExtrude","CAP_FACE",FACE,{"disambiguationData":[OSD([subQ5])],"isStart":false}),makeQuery(id+"F3.opExtrude","CAP_FACE",FACE,{"disambiguationData":[OSD([subQ4])],"isStart":true}),makeQuery(id+"F3.opExtrude","CAP_FACE",FACE,{"disambiguationData":[OSD([subQ4])],"isStart":false}),makeQuery(id+"F3.opExtrude","CAP_FACE",FACE,{"disambiguationData":[OSD([subQ3])],"isStart":true}),makeQuery(id+"F3.opExtrude","CAP_FACE",FACE,{"disambiguationData":[OSD([subQ3])],"isStart":false}),makeQuery(id+"F3.opExtrude","CAP_FACE",FACE,{"disambiguationData":[OSD([subQ2])],"isStart":true}),makeQuery(id+"F3.opExtrude","CAP_FACE",FACE,{"disambiguationData":[OSD([subQ2])],"isStart":false}),makeQuery(id+"F3.opExtrude","CAP_FACE",FACE,{"disambiguationData":[OSD([subQ1])],"isStart":true}),makeQuery(id+"F3.opExtrude","CAP_FACE",FACE,{"disambiguationData":[OSD([subQ1])],"isStart":false}),makeQuery(id+"F3.opExtrude","CAP_FACE",FACE,{"disambiguationData":[OSD([subQ0])],"isStart":true}),makeQuery(id+"F3.opExtrude","CAP_FACE",FACE,{"disambiguationData":[OSD([subQ0])],"isStart":false}),makeQuery(id+"F3.opExtrude","SWEPT_FACE",FACE,{"disambiguationData":[OSD([subQ10])]}),makeQuery(id+"F3.opExtrude","CAP_FACE",FACE,{"disambiguationData":[OSD([subQ10])],"isStart":true}),makeQuery(id+"F3.opExtrude","CAP_FACE",FACE,{"disambiguationData":[OSD([subQ10])],"isStart":false}),makeQuery(id+"F3.opExtrude","SWEPT_FACE",FACE,{"disambiguationData":[OSD([subQ11])]}),makeQuery(id+"F3.opExtrude","CAP_FACE",FACE,{"disambiguationData":[OSD([subQ11])],"isStart":true}),makeQuery(id+"F3.opExtrude","CAP_FACE",FACE,{"disambiguationData":[OSD([subQ11])],"isStart":false})])],"derivedFrom":makeQuery(id+"F1.opRevolve","SWEPT_FACE",FACE,{"disambiguationData":[OSD([sQuery(id+"F0.wireOp",EDGE,"E27"),sQuery(id+"F0.wireOp",EDGE,"E52.MirrorCS")])]})});}
            extrude(context, id + "F17", {"entities" : qUnion([Q0]), "operationType" : NewBodyOperationType.REMOVE, "depth" : 4 * mm, "offsetDistance" : 25 * mm, "hasSecondDirection" : true, "secondDirectionBound" : SecondDirectionBoundingType.UP_TO_SURFACE, "secondDirectionOppositeDirection" : true, "secondDirectionDepth" : 25 * mm, "secondDirectionBoundEntityFace" : qUnion([Q1])});
        }
    });
